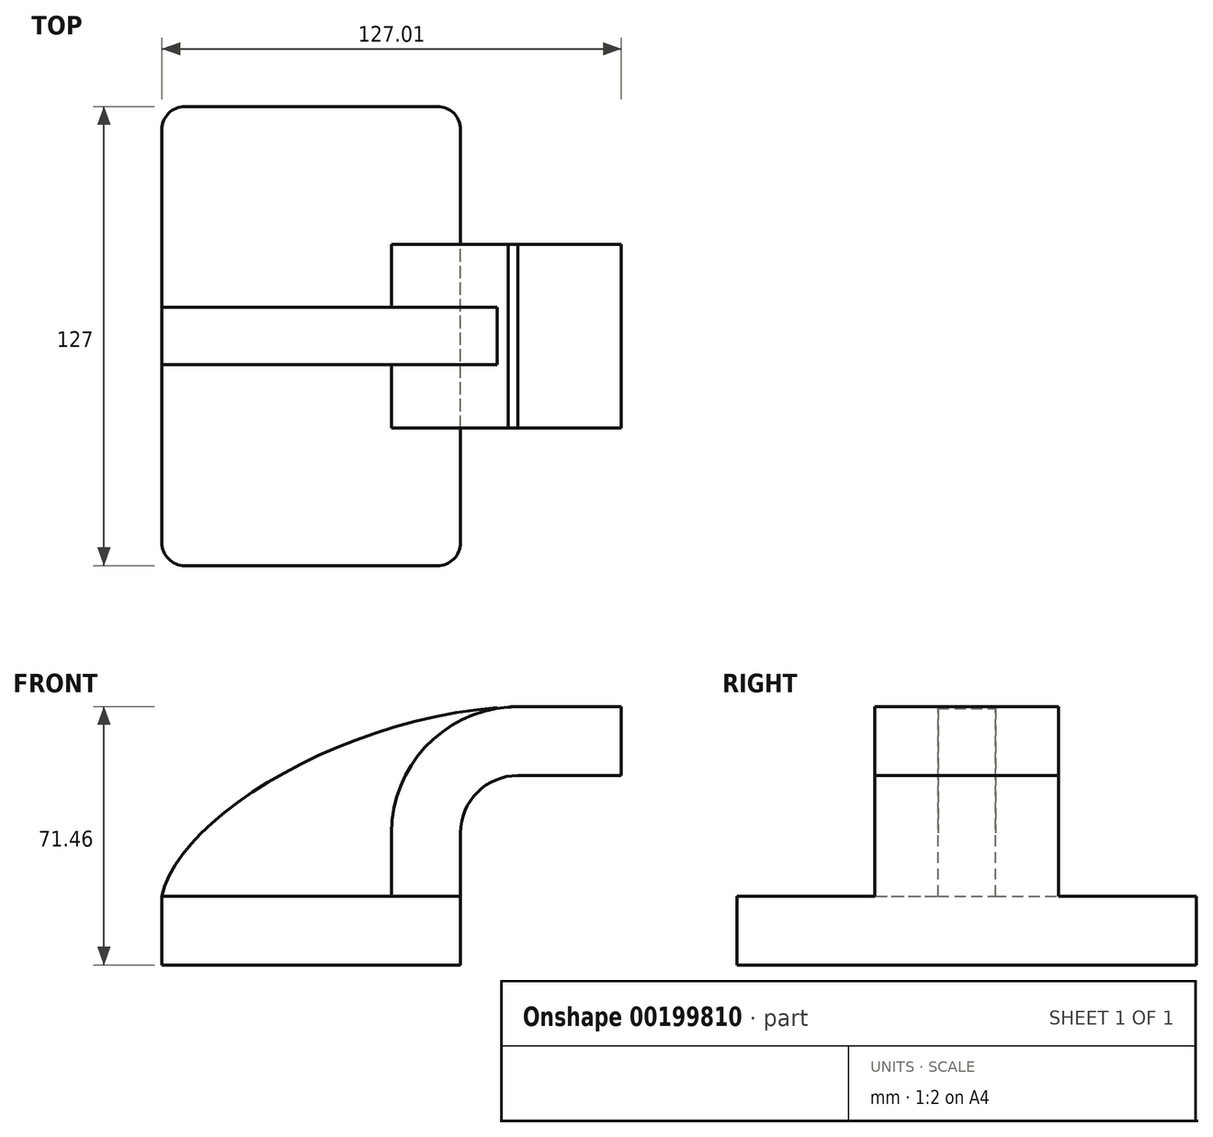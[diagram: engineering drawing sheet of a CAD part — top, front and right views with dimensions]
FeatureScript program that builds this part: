
annotation { "Feature Type Name" : "Feature", "Feature Type Description" : "" }
export const myFeature = defineFeature(function(context is Context, id is Id, definition is map)
    precondition{}
    {
        {
            var Q0;
            Q0=qCreatedBy(makeId("Front.planeOp"),FACE);
            var sketch = newSketch(context, id + "F0", { "sketchPlane" : qUnion([Q0])});
            skLineSegment(sketch, "E0.bottom", {"start": v(-41.27, -9.53) * mm, "end": v(41.28, -9.53) * mm});
            skLineSegment(sketch, "E0.top", {"start": v(-41.28, 9.52) * mm, "end": v(41.28, 9.52) * mm});
            skLineSegment(sketch, "E0.left", {"start": v(-41.28, -9.53) * mm, "end": v(-41.28, 9.52) * mm});
            skLineSegment(sketch, "E0.right", {"start": v(41.28, -9.53) * mm, "end": v(41.28, 9.52) * mm});
            skPoint(sketch, "E0.middle", {"position": v(0, 0) * mm});
            skLineSegment(sketch, "E1.bottom", {"start": v(51.44, 38.1) * mm, "end": v(102.24, 38.1) * mm});
            skLineSegment(sketch, "E1.top", {"start": v(51.44, 66.67) * mm, "end": v(102.24, 66.67) * mm});
            skLineSegment(sketch, "E1.left", {"start": v(51.44, 38.1) * mm, "end": v(51.44, 66.67) * mm});
            skLineSegment(sketch, "E1.right", {"start": v(102.24, 38.1) * mm, "end": v(102.24, 66.67) * mm});
            skPoint(sketch, "E1.middle", {"position": v(76.84, 52.39) * mm});
            skLineSegment(sketch, "E2", {"start": v(41.28, 9.52) * mm, "end": v(41.28, 27) * mm});
            skArc(sketch, "E3", {"start": v(41.27, 27) * mm, "mid": v(45.92, 38.23) * mm, "end": v(57.15, 42.88) * mm});
            skLineSegment(sketch, "E4", {"start": v(57.15, 42.88) * mm, "end": v(85.73, 42.88) * mm});
            skLineSegment(sketch, "E5.0", {"start": v(57.15, 61.93) * mm, "end": v(85.73, 61.93) * mm});
            skArc(sketch, "E5.1", {"start": v(22.22, 27) * mm, "mid": v(32.45, 51.7) * mm, "end": v(57.15, 61.93) * mm});
            skLineSegment(sketch, "E5.2", {"start": v(22.22, 9.52) * mm, "end": v(22.22, 27) * mm});
            skLineSegment(sketch, "E6", {"start": v(85.73, 42.88) * mm, "end": v(85.73, 61.93) * mm});
            skFitSpline(sketch, "E7", {"points": [v(-41.27, 9.52) * mm, v(57.15, 61.93) * mm], "startDerivative": vector(13.42, 66.36) * mm, "endDerivative": vector(137.56, 3.7) * mm});
            skSolve(sketch);
        }
        {
            var Q0;
            Q0=makeQuery(id+"F0.imprint","IMPRINT",FACE,{"disambiguationData":[TD([[makeQuery(id+"F0.imprint","IMPRINT",EDGE,{"derivedFrom":sQuery(id+"F0.wireOp",EDGE,"E0.bottom")}),1.0]])]});
            extrude(context, id + "F1", {"entities" : qUnion([Q0]), "endBound" : BoundingType.SYMMETRIC, "depth" : 127 * mm});
        }
        {
            var Q0;
            {var subQ1=sQuery(id+"F0.wireOp",EDGE,"E2");Q0=makeQuery(id+"F0.imprint","IMPRINT",FACE,{"disambiguationData":[TD([[makeQuery(id+"F0.imprint","IMPRINT",EDGE,{"derivedFrom":subQ1}),1.0]])]});}
            var Q1;
            {var subQ1=sQuery(id+"F0.wireOp",EDGE,"E4");Q1=makeQuery(id+"F0.imprint","IMPRINT",FACE,{"disambiguationData":[TD([[makeQuery(id+"F0.imprint","IMPRINT",EDGE,{"derivedFrom":subQ1}),1.0]])]});}
            extrude(context, id + "F2", {"entities" : qUnion([Q0, Q1]), "operationType" : NewBodyOperationType.ADD, "endBound" : BoundingType.SYMMETRIC, "depth" : 50.8 * mm});
        }
        {
            var Q0;
            {var subQ0=sQuery(id+"F0.wireOp",EDGE,"E5.2");Q0=makeQuery(id+"F0.imprint","IMPRINT",FACE,{"disambiguationData":[TD([[makeQuery(id+"F0.imprint","IMPRINT",EDGE,{"derivedFrom":subQ0}),1.0]])]});}
            extrude(context, id + "F3", {"entities" : qUnion([Q0]), "operationType" : NewBodyOperationType.ADD, "endBound" : BoundingType.SYMMETRIC, "depth" : 15.88 * mm});
        }
        {
            var Q0;
            Q0=makeQuery(id+"F1.opExtrude","CAP_EDGE",EDGE,{"disambiguationData":[OSD([sQuery(id+"F0.wireOp",EDGE,"E0.left")])],"isStart":false});
            var Q1;
            Q1=makeQuery(id+"F1.opExtrude","CAP_EDGE",EDGE,{"disambiguationData":[OSD([sQuery(id+"F0.wireOp",EDGE,"E0.right")])],"isStart":false});
            var Q2;
            Q2=makeQuery(id+"F1.opExtrude","CAP_EDGE",EDGE,{"disambiguationData":[OSD([sQuery(id+"F0.wireOp",EDGE,"E0.right")])],"isStart":true});
            var Q3;
            Q3=makeQuery(id+"F1.opExtrude","CAP_EDGE",EDGE,{"disambiguationData":[OSD([sQuery(id+"F0.wireOp",EDGE,"E0.left")])],"isStart":true});
            fillet(context, id + "F4", {"entities" : qUnion([Q0, Q1, Q2, Q3]), "radius" : 6.35 * mm, "tangentPropagation" : true, "allowEdgeOverflow" : false});
        }
    });
